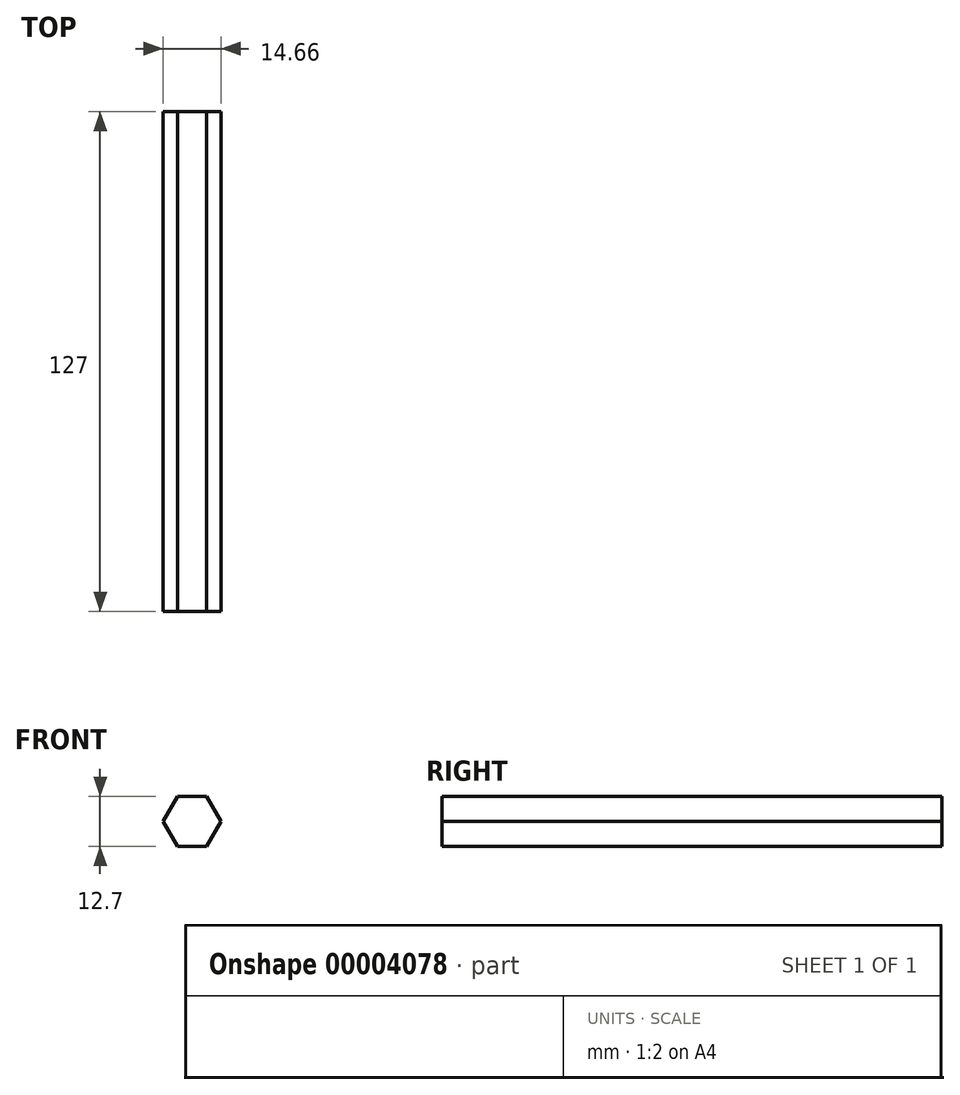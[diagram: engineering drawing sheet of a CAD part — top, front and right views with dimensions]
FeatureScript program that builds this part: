
annotation { "Feature Type Name" : "Feature", "Feature Type Description" : "" }
export const myFeature = defineFeature(function(context is Context, id is Id, definition is map)
    precondition{}
    {
        {
            var Q0;
            Q0=qCreatedBy(makeId("Front.planeOp"),FACE);
            var sketch = newSketch(context, id + "F0", { "sketchPlane" : qUnion([Q0])});
            skCircle(sketch, "E0.cCircle", {"center": v(0, 0) * mm, "radius": 6.35 * mm, "construction": true});
            skLineSegment(sketch, "E0.0", {"start": v(-3.67, 6.35) * mm, "end": v(3.67, 6.35) * mm});
            skLineSegment(sketch, "E0.1", {"start": v(3.67, 6.35) * mm, "end": v(7.33, 0) * mm});
            skLineSegment(sketch, "E0.2", {"start": v(7.33, 0) * mm, "end": v(3.67, -6.35) * mm});
            skLineSegment(sketch, "E0.3", {"start": v(3.67, -6.35) * mm, "end": v(-3.67, -6.35) * mm});
            skLineSegment(sketch, "E0.4", {"start": v(-3.67, -6.35) * mm, "end": v(-7.33, 0) * mm});
            skLineSegment(sketch, "E0.5", {"start": v(-7.33, 0) * mm, "end": v(-3.67, 6.35) * mm});
            skPoint(sketch, "E0.0.midPoint", {"position": v(0, 6.35) * mm});
            skSolve(sketch);
        }
        {
            var Q0;
            Q0=makeQuery(id+"F0.imprint","IMPRINT",FACE,{"disambiguationData":[TD([[makeQuery(id+"F0.imprint","IMPRINT",EDGE,{"derivedFrom":sQuery(id+"F0.wireOp",EDGE,"E0.0")}),-1.0]])]});
            extrude(context, id + "F1", {"entities" : qUnion([Q0]), "endBound" : BoundingType.SYMMETRIC, "depth" : 127 * mm});
        }
    });
